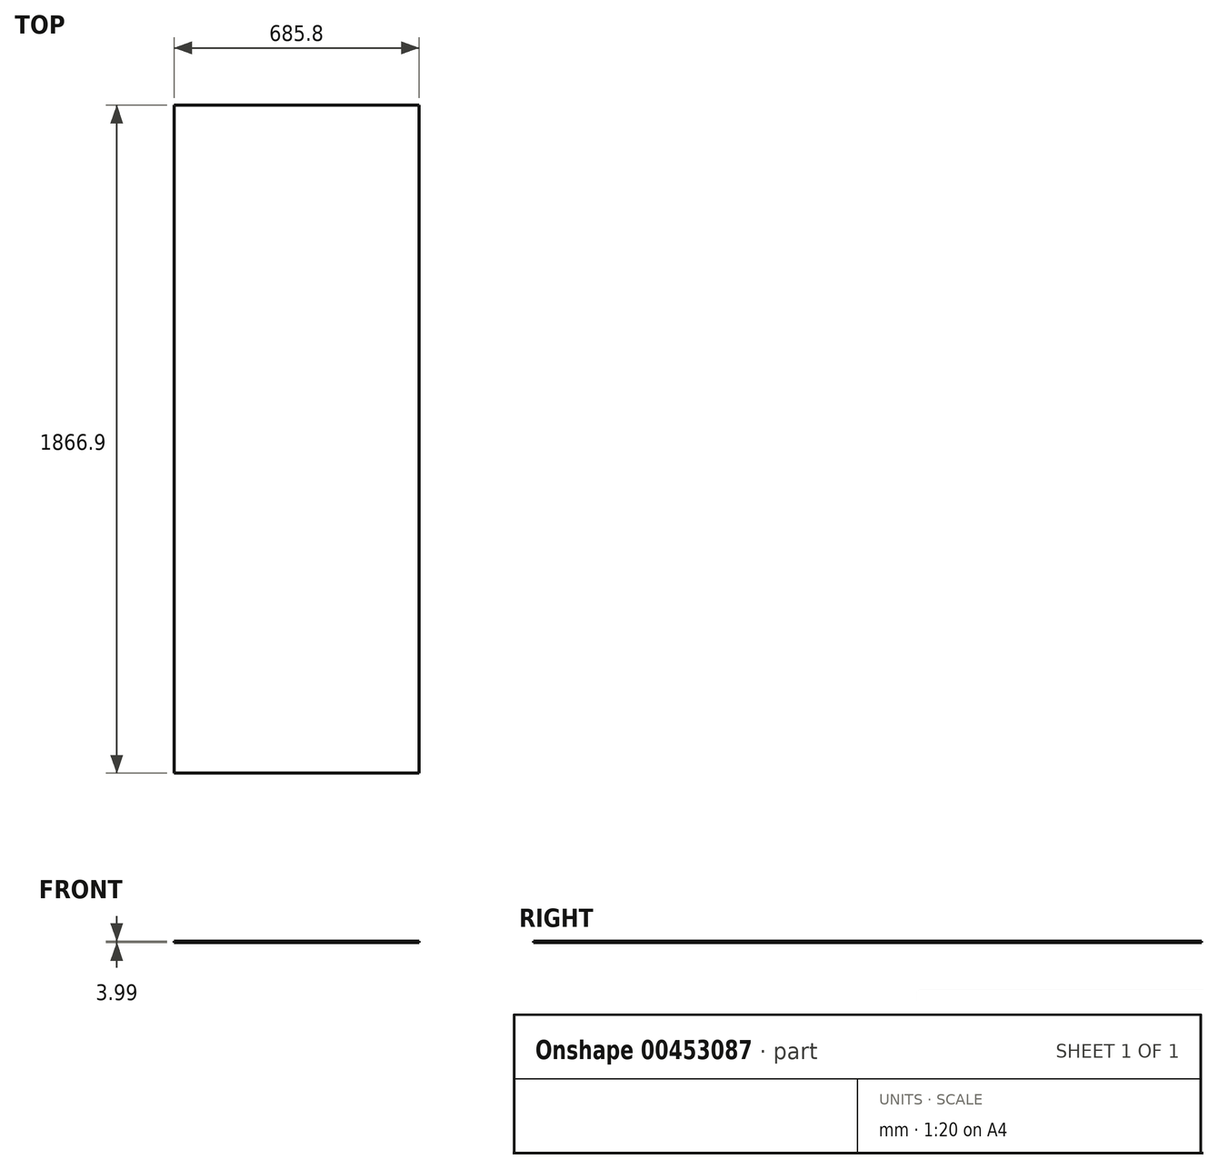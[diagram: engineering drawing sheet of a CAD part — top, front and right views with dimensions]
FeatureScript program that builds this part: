
annotation { "Feature Type Name" : "Feature", "Feature Type Description" : "" }
export const myFeature = defineFeature(function(context is Context, id is Id, definition is map)
    precondition{}
    {
        {
            var Q0;
            Q0=qCreatedBy(makeId("Top.planeOp"),FACE);
            var sketch = newSketch(context, id + "F0", { "sketchPlane" : qUnion([Q0])});
            skLineSegment(sketch, "E0.bottom", {"start": v(342.9, 933.45) * mm, "end": v(-342.9, 933.45) * mm});
            skLineSegment(sketch, "E0.top", {"start": v(342.9, -933.45) * mm, "end": v(-342.9, -933.45) * mm});
            skLineSegment(sketch, "E0.left", {"start": v(342.9, 933.45) * mm, "end": v(342.9, -933.45) * mm});
            skLineSegment(sketch, "E0.right", {"start": v(-342.9, 933.45) * mm, "end": v(-342.9, -933.45) * mm});
            skPoint(sketch, "E0.middle", {"position": v(0, 0) * mm});
            skSolve(sketch);
        }
        {
            var Q0;
            Q0 = qSketchRegion(id + "F0", true);
            extrude(context, id + "F1", {"entities" : qUnion([Q0]), "depth" : 4 * mm, "offsetDistance" : 25.4 * mm});
        }
    });
